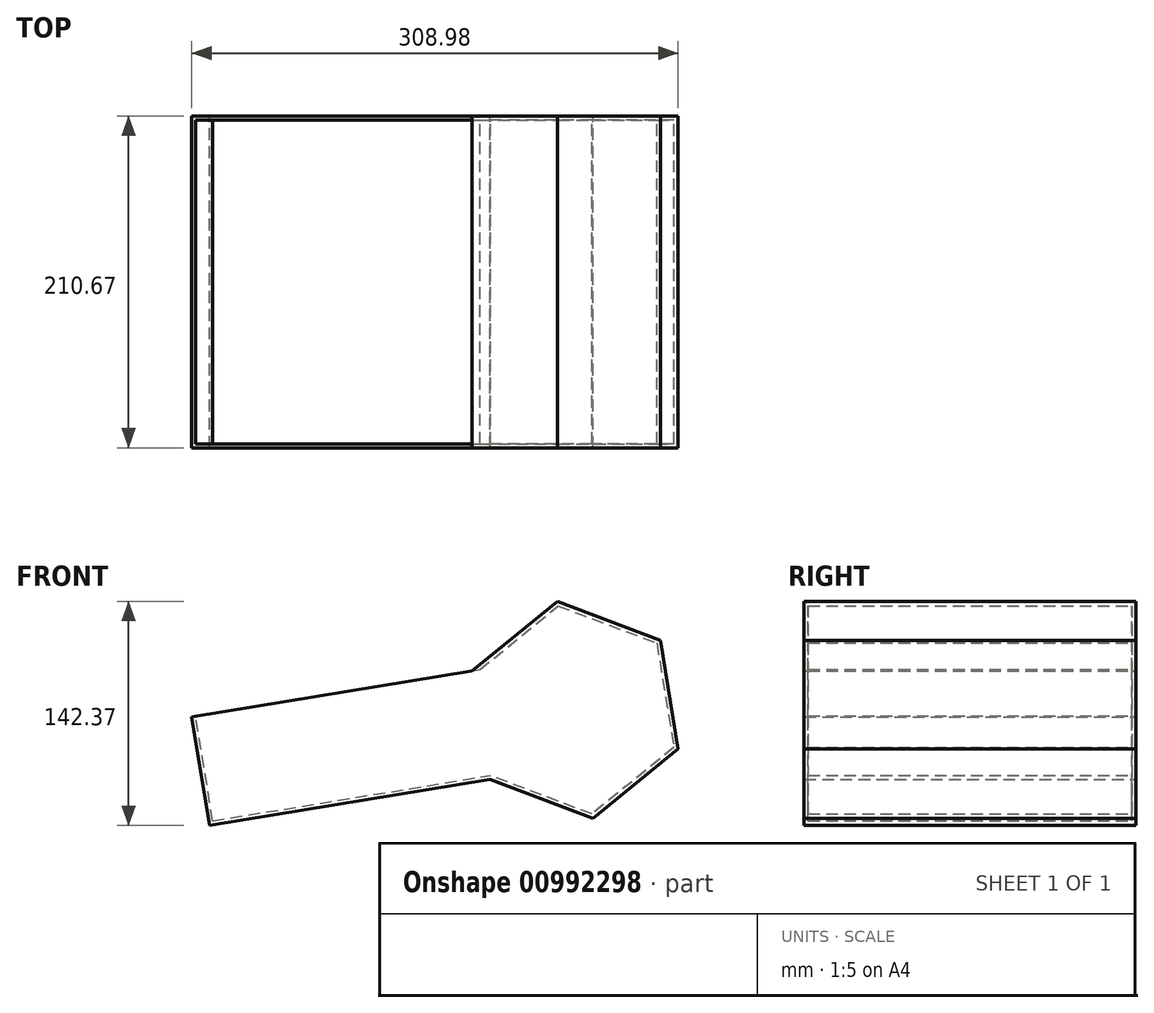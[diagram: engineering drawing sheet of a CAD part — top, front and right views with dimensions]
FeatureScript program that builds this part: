
annotation { "Feature Type Name" : "Feature", "Feature Type Description" : "" }
export const myFeature = defineFeature(function(context is Context, id is Id, definition is map)
    precondition{}
    {
        {
            var Q0;
            Q0=qCreatedBy(makeId("Front.planeOp"),FACE);
            var sketch = newSketch(context, id + "F0", { "sketchPlane" : qUnion([Q0])});
            skCircle(sketch, "E0.cCircle", {"center": v(0, 0) * mm, "radius": 69.94 * mm, "construction": true});
            skLineSegment(sketch, "E0.0", {"start": v(65.41, -24.76) * mm, "end": v(11.26, -69.03) * mm});
            skLineSegment(sketch, "E0.1", {"start": v(11.26, -69.03) * mm, "end": v(-54.15, -44.27) * mm});
            skLineSegment(sketch, "E0.2", {"start": v(-54.15, -44.27) * mm, "end": v(-65.41, 24.76) * mm});
            skLineSegment(sketch, "E0.3", {"start": v(-65.41, 24.76) * mm, "end": v(-11.26, 69.03) * mm});
            skLineSegment(sketch, "E0.4", {"start": v(-11.26, 69.03) * mm, "end": v(54.15, 44.27) * mm});
            skLineSegment(sketch, "E0.5", {"start": v(54.15, 44.27) * mm, "end": v(65.41, -24.76) * mm});
            skSolve(sketch);
        }
        {
            var Q0;
            Q0=makeQuery(id+"F0.imprint","IMPRINT",FACE,{"disambiguationData":[TD([[makeQuery(id+"F0.imprint","IMPRINT",EDGE,{"derivedFrom":sQuery(id+"F0.wireOp",EDGE,"E0.0")}),-1.0]])]});
            extrude(context, id + "F1", {"entities" : qUnion([Q0]), "depth" : 210.67 * mm, "offsetDistance" : 25.4 * mm});
        }
        {
            var Q0;
            Q0=makeQuery(id+"F1.opExtrude","SWEPT_FACE",FACE,{"disambiguationData":[OSD([sQuery(id+"F0.wireOp",EDGE,"E0.2")])]});
            extrude(context, id + "F2", {"entities" : qUnion([Q0]), "operationType" : NewBodyOperationType.ADD, "depth" : 180.52 * mm, "offsetDistance" : 25.4 * mm});
        }
        {
            var Q0;
            {var subQ0=sQuery(id+"F0.wireOp",EDGE,"E0.2");Q0=makeQuery(id+"F2.boolean.opBoolean","MERGE",FACE,{"derivedFrom":[makeQuery(id+"F1.opExtrude","CAP_FACE",FACE,{"disambiguationData":[OSD([sQuery(id+"F0.wireOp",EDGE,"E0.0"),sQuery(id+"F0.wireOp",EDGE,"E0.1"),subQ0,sQuery(id+"F0.wireOp",EDGE,"E0.3"),sQuery(id+"F0.wireOp",EDGE,"E0.4"),sQuery(id+"F0.wireOp",EDGE,"E0.5")])],"isStart":false}),makeQuery(id+"F2.opExtrude","SWEPT_FACE",FACE,{"disambiguationData":[OSD([subQ0]),TDD([makeQuery(id+"F1.opExtrude","CAP_EDGE",EDGE,{"disambiguationData":[OSD([subQ0])],"isStart":false})])]})]});}
            var sketch = newSketch(context, id + "F3", { "sketchPlane" : qUnion([Q0])});
            skCircle(sketch, "E1", {"center": v(0, 0) * mm, "radius": 34.97 * mm});
            skSolve(sketch);
        }
        {
            var Q0;
            Q0=makeQuery(id+"F2.opExtrude","SWEPT_FACE",FACE,{"disambiguationData":[OSD([sQuery(id+"F0.wireOp",EDGE,"E0.2"),sQuery(id+"F0.wireOp",EDGE,"E0.3")])]});
            shell(context, id + "F4", {"entities" : qUnion([Q0]), "thickness" : 2.54 * mm});
        }
        {
            var Q0;
            Q0=sQuery(id+"F3.wireOp",EDGE,"E1");
            extrude(context, id + "F5", {"bodyType" : ToolBodyType.SURFACE, "surfaceEntities" : qUnion([Q0]), "oppositeDirection" : true, "depth" : 211.76 * mm, "offsetDistance" : 25.4 * mm});
        }
    });
